# Revit family: Furniture_Other_Sjobergs_Duplex_1-station
name_source: partatom
category: Furniture
revit_build: Autodesk Revit 2018 (Build: 20170223_1515(x64)
units: mm (PartAtom-declared; Revit-internal decimal feet)

## family parameters
Always vertical = Yes
Cut with Voids When Loaded = No
OmniClass Number = 23.40.70.14
OmniClass Title = Retail and Commercial Equipment and Furnishings
Room Calculation Point = No
Shared = No
Work Plane-Based = No

## types (1)
- Duplex, 1-station
    AssetType = Movable
    BIMObjectName = Furniture_Other_Sjobergs_Duplex_1-station
    Brand = Sjöbergs
    Category = Workbench
    Collection = Duplex
    Color = Wooden
    Cost = 0 $
    Description = SJÖBERGS DUPLEX is the perfect electrical workplace for one person, whether right- or left- handed. The height is easy to adjust, operates with a european standard plug-in cord and offers easy access to wheelchair users.
The laquered beech top has a thickness of 60 mm and includes a heavily contstructed vise, making this bench exceptionally flexible and sturdy. Add foot for even more stability, art.no. 33342.
    DurationUnit = Year
    Features = The laquered beech top has a thickness of 60 mm and includes a heavily contstructed vise, making this bench exceptionally flexible and sturdy. Add foot for even more stability, art.no. 33342.
    Finish = Lacquered beech.
    IfcExportAs = IfcFurnishingElementType
    IfcExportType = TABLE
    MainColor = Wooden
    Manufacturer = Sjöbergs
    ManufacturerName = Sjöbergs
    ManufacturerURL = https://www.sjobergs.se
    Material = Wood, metal
    Model = Duplex, 1-station
    ModelReference = 33082
    NBSDescription = School art, design and technology tables and workbenches;
    NBSReference = 45-35-20/320
    Name = Duplex_1-station
    NominalDepth = 430 mm  [stored 1.41076 ft]
    Nominal_Height = 1000 mm  [stored 3.28084 ft]
    Nominal_Width = 1200 mm
    ProductDatasheet = https://sjobergs.se
    ProductInformation = SJÖBERGS DUPLEX is the perfect electrical workplace for one person, whether right- or left- handed. The height is easy to adjust, operates with a european standard plug-in cord and offers easy access to wheelchair users.
The laquered beech top has a thickness of 60 mm and includes a heavily contstructed vise, making this bench exceptionally flexible and sturdy. Add foot for even more stability, art.no. 33342.
    Shape = Sculptured
    Size = 1200x430x700-900 mm
    TableMainMaterial = Beech
    TableSecondaryMaterial = Stainless Steel
    URL = https://sjobergs.se
    Uniclass2 = Pr_40_50_21
    Uniclass2015Description = Desks, Tables And Worktops
    Uniclass2015Reference = Pr_40_50_21_76
    Version = 1
    VersionDate = 04/04/2022
    WarrantyDurationUnit = Year
    Weight = 50 Kg

note: [stored X ft] marks values corroborated as IEEE doubles in the binary element streams (Revit-internal decimal feet)

## geometry (parser evidence)
native form markers: Sweep x6
no freeform markers — native parametric forms only
